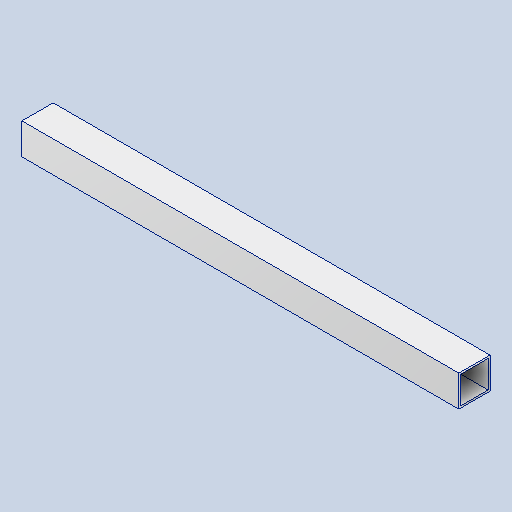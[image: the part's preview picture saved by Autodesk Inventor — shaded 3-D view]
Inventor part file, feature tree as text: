
AUTODESK INVENTOR PART (.ipt)
format: ipt  version: 2025.1 (Build 291241020, 241B)  size: 113,664 bytes
history: native  units: in
note: dims shown in document units (in); Inventor stores cm internally (conversion verified against a paired STEP export)
features: other x14, extrude x1, sketch x1
ambient origin geometry x8: Origin, YZ Plane, XZ Plane, XY Plane, X Axis, Y Axis, Z Axis, Center Point
bodies: Solid1 (feature_tree)
feature tree (16):
  other  "Table"
  other  "Part1-01"
  other  "Part1-02"
  other  "Part1-03"
  other  "Part1-04"
  other  "Part1-05"
  other  "aluminumextrusiontool-16"
  other  "aluminumextrusiontool-17-L1"
  other  "aluminumextrusiontool-17_l2"
  other  "aluminumextrusiontool-17-11in"
  other  "aluminumextrusiontool-17-10.6in"
  other  "aluminumextrusiontool-17-13in"
  other  "aluminumextrusiontool-17-13.31255in"
  other  "aluminumextrusiontool-17-7.9"
  extrude  "Extrusion1"  Depth=14.0in TaperAngle=0.0deg
  sketch  "Sketch1"  dims[d0=1.0in d1=14.0in d2=0.0in d24=0.0625in d25=0.0625in d26=0.0625in d27=0.0625in]
